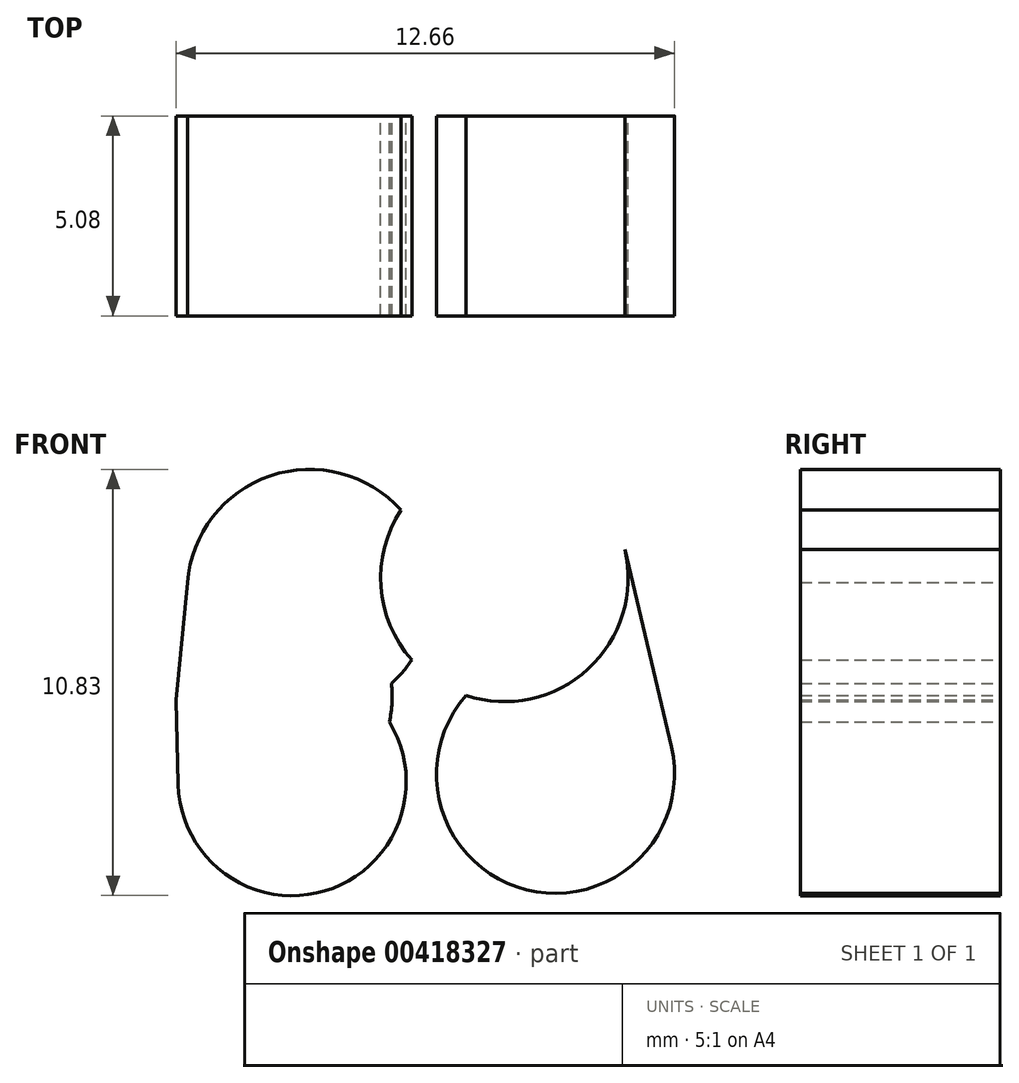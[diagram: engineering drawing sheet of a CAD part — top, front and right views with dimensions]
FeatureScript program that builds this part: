
annotation { "Feature Type Name" : "Feature", "Feature Type Description" : "" }
export const myFeature = defineFeature(function(context is Context, id is Id, definition is map)
    precondition{}
    {
        {
            var Q0;
            Q0=qCreatedBy(makeId("Front.planeOp"),FACE);
            var sketch = newSketch(context, id + "F0", { "sketchPlane" : qUnion([Q0])});
            skCircle(sketch, "E0", {"center": v(-6.69, -4.05) * mm, "radius": 2.9 * mm});
            skCircle(sketch, "E1", {"center": v(0, -3.85) * mm, "radius": 3.02 * mm});
            skLineSegment(sketch, "E2", {"start": v(-6.66, -6.94) * mm, "end": v(0, -6.88) * mm});
            skCircle(sketch, "E3", {"center": v(-6.9, -1.9) * mm, "radius": 2.75 * mm});
            skLineSegment(sketch, "E4", {"start": v(-9.64, -1.97) * mm, "end": v(-9.58, -4.12) * mm});
            skCircle(sketch, "E5", {"center": v(-6.25, 0.77) * mm, "radius": 3.12 * mm});
            skLineSegment(sketch, "E6", {"start": v(-9.35, 1.01) * mm, "end": v(-9.64, -1.97) * mm});
            skCircle(sketch, "E7", {"center": v(-1.3, 1.13) * mm, "radius": 3.14 * mm});
            skLineSegment(sketch, "E8", {"start": v(1.76, 1.85) * mm, "end": v(2.94, -3.16) * mm});
            skSolve(sketch);
        }
        {
            var Q0;
            {var subQ0=sQuery(id+"F0.wireOp",EDGE,"E5");var subQ2=sQuery(id+"F0.wireOp",EDGE,"E3");var subQ3=makeQuery(id+"F0.imprint","INTERSECT",VERTEX,{"disambiguationData":[OD(0.0)],"derivedFrom":[subQ2,subQ0]});Q0=makeQuery(id+"F0.imprint","IMPRINT",FACE,{"disambiguationData":[TD([[makeQuery(id+"F0.imprint","IMPRINT",EDGE,{"disambiguationData":[TD([[subQ3,1.0]])],"derivedFrom":subQ2}),-1.0]])]});}
            var Q1;
            {var subQ0=sQuery(id+"F0.wireOp",EDGE,"E5");var subQ1=sQuery(id+"F0.wireOp",EDGE,"E0");var subQ2=makeQuery(id+"F0.imprint","INTERSECT",VERTEX,{"disambiguationData":[OD(0.0)],"derivedFrom":[subQ1,subQ0]});Q1=makeQuery(id+"F0.imprint","IMPRINT",FACE,{"disambiguationData":[TD([[makeQuery(id+"F0.imprint","IMPRINT",EDGE,{"disambiguationData":[TD([[subQ2,-1.0]])],"derivedFrom":subQ1}),-1.0]])]});}
            var Q2;
            {var subQ0=sQuery(id+"F0.wireOp",EDGE,"E5");var subQ1=sQuery(id+"F0.wireOp",EDGE,"E0");var subQ2=makeQuery(id+"F0.imprint","INTERSECT",VERTEX,{"disambiguationData":[OD(1.0)],"derivedFrom":[subQ1,subQ0]});Q2=makeQuery(id+"F0.imprint","IMPRINT",FACE,{"disambiguationData":[TD([[makeQuery(id+"F0.imprint","IMPRINT",EDGE,{"disambiguationData":[TD([[subQ2,-1.0]])],"derivedFrom":subQ1}),-1.0]])]});}
            var Q3;
            {var subQ0=sQuery(id+"F0.wireOp",EDGE,"E0");var subQ1=makeQuery(id+"F0.imprint","INTERSECT",VERTEX,{"derivedFrom":[subQ0,sQuery(id+"F0.wireOp",EDGE,"E4")]});Q3=makeQuery(id+"F0.imprint","IMPRINT",FACE,{"disambiguationData":[TD([[makeQuery(id+"F0.imprint","IMPRINT",EDGE,{"disambiguationData":[TD([[subQ1,1.0]])],"derivedFrom":subQ0}),1.0]])]});}
            var Q4;
            {var subQ0=sQuery(id+"F0.wireOp",EDGE,"E5");var subQ1=sQuery(id+"F0.wireOp",EDGE,"E0");var subQ2=makeQuery(id+"F0.imprint","INTERSECT",VERTEX,{"disambiguationData":[OD(0.0)],"derivedFrom":[subQ1,subQ0]});Q4=makeQuery(id+"F0.imprint","IMPRINT",FACE,{"disambiguationData":[TD([[makeQuery(id+"F0.imprint","IMPRINT",EDGE,{"disambiguationData":[TD([[subQ2,1.0]])],"derivedFrom":subQ1}),1.0]])]});}
            var Q5;
            {var subQ0=sQuery(id+"F0.wireOp",EDGE,"E4");Q5=makeQuery(id+"F0.imprint","IMPRINT",FACE,{"disambiguationData":[TD([[makeQuery(id+"F0.imprint","IMPRINT",EDGE,{"derivedFrom":subQ0}),1.0]])]});}
            var Q6;
            {var subQ0=sQuery(id+"F0.wireOp",EDGE,"E6");var subQ1=sQuery(id+"F0.wireOp",EDGE,"E3");var subQ2=makeQuery(id+"F0.imprint","INTERSECT",VERTEX,{"derivedFrom":[subQ1,subQ0]});Q6=makeQuery(id+"F0.imprint","IMPRINT",FACE,{"disambiguationData":[TD([[makeQuery(id+"F0.imprint","IMPRINT",EDGE,{"disambiguationData":[TD([[subQ2,1.0]])],"derivedFrom":subQ1}),-1.0]])]});}
            var Q7;
            {var subQ0=sQuery(id+"F0.wireOp",EDGE,"E5");var subQ1=sQuery(id+"F0.wireOp",EDGE,"E0");var subQ2=makeQuery(id+"F0.imprint","INTERSECT",VERTEX,{"disambiguationData":[OD(0.0)],"derivedFrom":[subQ1,subQ0]});Q7=makeQuery(id+"F0.imprint","IMPRINT",FACE,{"disambiguationData":[TD([[makeQuery(id+"F0.imprint","IMPRINT",EDGE,{"disambiguationData":[TD([[subQ2,-1.0]])],"derivedFrom":subQ1}),1.0]])]});}
            var Q8;
            {var subQ0=sQuery(id+"F0.wireOp",EDGE,"E5");var subQ1=sQuery(id+"F0.wireOp",EDGE,"E0");var subQ2=makeQuery(id+"F0.imprint","INTERSECT",VERTEX,{"disambiguationData":[OD(0.0)],"derivedFrom":[subQ1,subQ0]});Q8=makeQuery(id+"F0.imprint","IMPRINT",FACE,{"disambiguationData":[TD([[makeQuery(id+"F0.imprint","IMPRINT",EDGE,{"disambiguationData":[TD([[subQ2,1.0]])],"derivedFrom":subQ1}),-1.0]])]});}
            var Q9;
            {var subQ5=sQuery(id+"F0.wireOp",EDGE,"E2");Q9=makeQuery(id+"F0.imprint","IMPRINT",FACE,{"disambiguationData":[TD([[makeQuery(id+"F0.imprint","IMPRINT",EDGE,{"derivedFrom":subQ5}),1.0]])]});}
            var Q10;
            {var subQ0=sQuery(id+"F0.wireOp",EDGE,"E1");var subQ1=makeQuery(id+"F0.imprint","INTERSECT",VERTEX,{"derivedFrom":[subQ0,sQuery(id+"F0.wireOp",EDGE,"E8")]});Q10=makeQuery(id+"F0.imprint","IMPRINT",FACE,{"disambiguationData":[TD([[makeQuery(id+"F0.imprint","IMPRINT",EDGE,{"disambiguationData":[TD([[subQ1,-1.0]])],"derivedFrom":subQ0}),1.0]])]});}
            var Q11;
            {var subQ0=sQuery(id+"F0.wireOp",EDGE,"E7");var subQ1=sQuery(id+"F0.wireOp",EDGE,"E1");var subQ2=makeQuery(id+"F0.imprint","INTERSECT",VERTEX,{"disambiguationData":[OD(0.0)],"derivedFrom":[subQ1,subQ0]});Q11=makeQuery(id+"F0.imprint","IMPRINT",FACE,{"disambiguationData":[TD([[makeQuery(id+"F0.imprint","IMPRINT",EDGE,{"disambiguationData":[TD([[subQ2,-1.0]])],"derivedFrom":subQ1}),1.0]])]});}
            var Q12;
            {var subQ0=sQuery(id+"F0.wireOp",EDGE,"E7");var subQ1=sQuery(id+"F0.wireOp",EDGE,"E5");var subQ2=makeQuery(id+"F0.imprint","INTERSECT",VERTEX,{"disambiguationData":[OD(0.0)],"derivedFrom":[subQ1,subQ0]});Q12=makeQuery(id+"F0.imprint","IMPRINT",FACE,{"disambiguationData":[TD([[makeQuery(id+"F0.imprint","IMPRINT",EDGE,{"disambiguationData":[TD([[subQ2,1.0]])],"derivedFrom":subQ1}),1.0]])]});}
            var Q13;
            {var subQ0=sQuery(id+"F0.wireOp",EDGE,"E7");var subQ1=sQuery(id+"F0.wireOp",EDGE,"E1");var subQ5=makeQuery(id+"F0.imprint","INTERSECT",VERTEX,{"disambiguationData":[OD(0.0)],"derivedFrom":[subQ1,subQ0]});Q13=makeQuery(id+"F0.imprint","IMPRINT",FACE,{"disambiguationData":[TD([[makeQuery(id+"F0.imprint","IMPRINT",EDGE,{"disambiguationData":[TD([[subQ5,-1.0]])],"derivedFrom":subQ1}),-1.0]])]});}
            var Q14;
            {var subQ0=sQuery(id+"F0.wireOp",EDGE,"E8");Q14=makeQuery(id+"F0.imprint","IMPRINT",FACE,{"disambiguationData":[TD([[makeQuery(id+"F0.imprint","IMPRINT",EDGE,{"derivedFrom":subQ0}),-1.0]])]});}
            extrude(context, id + "F1", {"entities" : qUnion([Q0, Q1, Q2, Q3, Q4, Q5, Q6, Q7, Q8, Q9, Q10, Q11, Q12, Q13, Q14]), "depth" : 5.08 * mm});
        }
    });
